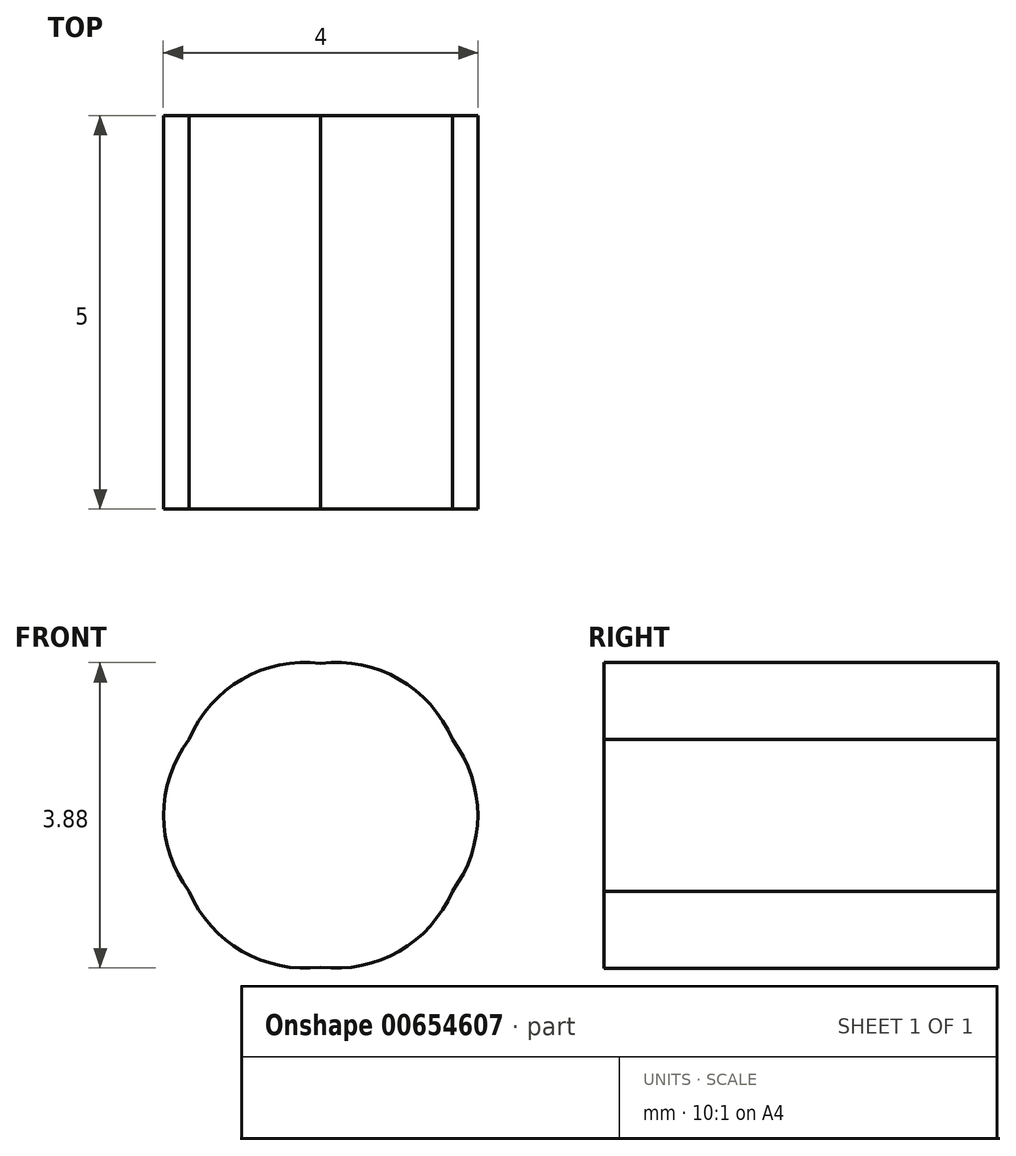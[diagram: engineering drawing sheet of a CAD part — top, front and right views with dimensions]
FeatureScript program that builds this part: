
annotation { "Feature Type Name" : "Feature", "Feature Type Description" : "" }
export const myFeature = defineFeature(function(context is Context, id is Id, definition is map)
    precondition{}
    {
        {
            var Q0;
            Q0=qCreatedBy(makeId("Front.planeOp"),FACE);
            var sketch = newSketch(context, id + "F0", { "sketchPlane" : qUnion([Q0])});
            skCircle(sketch, "E0", {"center": v(0, 0) * mm, "radius": 2 * mm});
            skArc(sketch, "E1", {"start": v(0, 1.93) * mm, "mid": v(-1, 1.73) * mm, "end": v(-1.67, 0.96) * mm});
            skCircle(sketch, "E2", {"center": v(0, 0) * mm, "radius": 0.4 * mm, "construction": true});
            skLineSegment(sketch, "E3", {"start": v(0, 0) * mm, "end": v(-0.2, 0.34) * mm});
            skLineSegment(sketch, "E4", {"start": v(0, 0) * mm, "end": v(0.2, 0.34) * mm});
            skLineSegment(sketch, "E5", {"start": v(0, 0) * mm, "end": v(0.4, 0) * mm});
            skLineSegment(sketch, "E6", {"start": v(0, 0) * mm, "end": v(0.2, -0.34) * mm});
            skLineSegment(sketch, "E7", {"start": v(0, 0) * mm, "end": v(-0.4, 0) * mm});
            skLineSegment(sketch, "E8", {"start": v(0, 0) * mm, "end": v(-0.2, -0.34) * mm});
            skArc(sketch, "E9", {"start": v(-1.67, 0.96) * mm, "mid": v(-2, 0) * mm, "end": v(-1.67, -0.96) * mm});
            skArc(sketch, "E10", {"start": v(-1.67, -0.96) * mm, "mid": v(-1, -1.73) * mm, "end": v(0, -1.93) * mm});
            skArc(sketch, "E11", {"start": v(0, -1.93) * mm, "mid": v(1, -1.73) * mm, "end": v(1.67, -0.96) * mm});
            skArc(sketch, "E12", {"start": v(1.67, -0.96) * mm, "mid": v(2, 0) * mm, "end": v(1.67, 0.96) * mm});
            skArc(sketch, "E13.trimOffspring", {"start": v(1.67, 0.96) * mm, "mid": v(1, 1.73) * mm, "end": v(0, 1.93) * mm});
            skSolve(sketch);
        }
        {
            var Q0;
            Q0=makeQuery(id+"F0.imprint","IMPRINT",FACE,{"disambiguationData":[TD([[makeQuery(id+"F0.imprint","IMPRINT",EDGE,{"derivedFrom":sQuery(id+"F0.wireOp",EDGE,"E9")}),1.0]])]});
            extrude(context, id + "F1", {"entities" : qUnion([Q0]), "depth" : 5 * mm, "offsetDistance" : 25.4 * mm});
        }
    });
